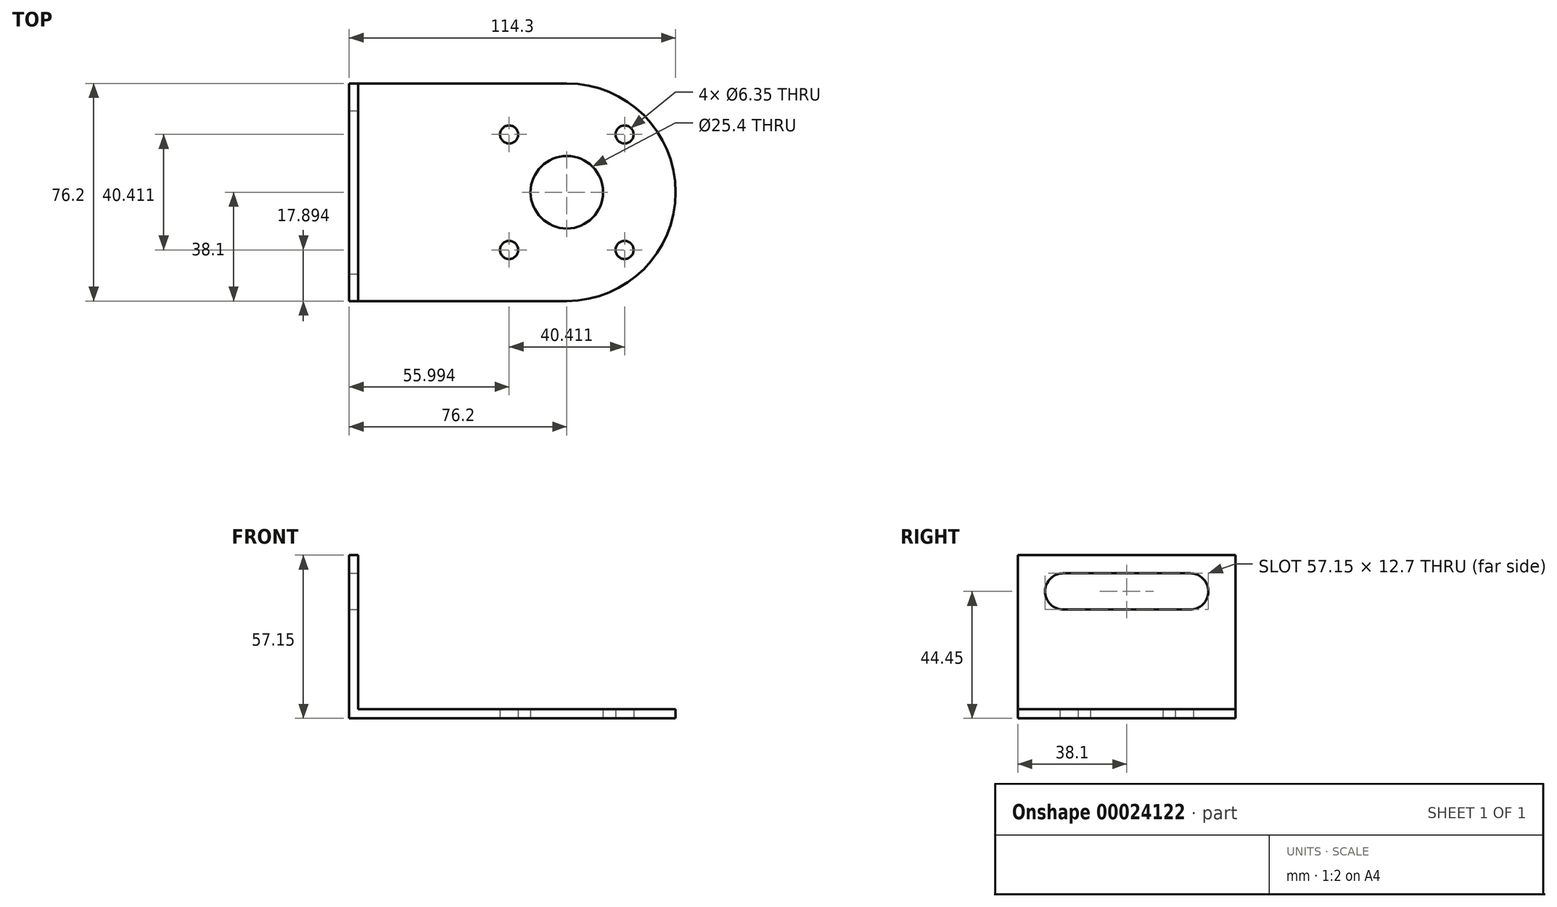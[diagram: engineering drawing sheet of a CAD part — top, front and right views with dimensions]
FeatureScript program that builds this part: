
annotation { "Feature Type Name" : "Feature", "Feature Type Description" : "" }
export const myFeature = defineFeature(function(context is Context, id is Id, definition is map)
    precondition{}
    {
        {
            var Q0;
            Q0=qCreatedBy(makeId("Top.planeOp"),FACE);
            var sketch = newSketch(context, id + "F0", { "sketchPlane" : qUnion([Q0])});
            skLineSegment(sketch, "E0", {"start": v(-76.2, 76.2) * mm, "end": v(-76.2, 0) * mm});
            skLineSegment(sketch, "E1", {"start": v(-76.2, 0) * mm, "end": v(0, 0) * mm});
            skLineSegment(sketch, "E2", {"start": v(0, 0) * mm, "end": v(0, 76.2) * mm, "construction": true});
            skLineSegment(sketch, "E3", {"start": v(0, 76.2) * mm, "end": v(-76.2, 76.2) * mm});
            skArc(sketch, "E4", {"start": v(0, 0) * mm, "mid": v(38.1, 38.1) * mm, "end": v(0, 76.2) * mm});
            skCircle(sketch, "E5", {"center": v(0, 38.1) * mm, "radius": 12.7 * mm});
            skCircle(sketch, "E6", {"center": v(0, 38.1) * mm, "radius": 28.58 * mm, "construction": true});
            skLineSegment(sketch, "E7", {"start": v(0, 38.1) * mm, "end": v(36.04, 74.14) * mm, "construction": true});
            skCircle(sketch, "E8", {"center": v(20.2, 58.3) * mm, "radius": 3.18 * mm});
            skCircle(sketch, "E9.1.0", {"center": v(-20.2, 58.3) * mm, "radius": 3.18 * mm});
            skCircle(sketch, "E9.2.0", {"center": v(-20.2, 17.9) * mm, "radius": 3.18 * mm});
            skCircle(sketch, "E9.3.0", {"center": v(20.2, 17.9) * mm, "radius": 3.18 * mm});
            skSolve(sketch);
        }
        {
            var Q0;
            Q0=makeQuery(id+"F0.imprint","IMPRINT",FACE,{"disambiguationData":[TD([[makeQuery(id+"F0.imprint","IMPRINT",EDGE,{"derivedFrom":sQuery(id+"F0.wireOp",EDGE,"E0")}),1.0]])]});
            extrude(context, id + "F1", {"entities" : qUnion([Q0]), "depth" : 3.17 * mm});
        }
        {
            var Q0;
            Q0=makeQuery(id+"F1.opExtrude","CAP_FACE",FACE,{"disambiguationData":[OSD([sQuery(id+"F0.wireOp",EDGE,"E0"),sQuery(id+"F0.wireOp",EDGE,"E1"),sQuery(id+"F0.wireOp",EDGE,"E3"),sQuery(id+"F0.wireOp",EDGE,"E4"),sQuery(id+"F0.wireOp",EDGE,"E5"),sQuery(id+"F0.wireOp",EDGE,"E8"),sQuery(id+"F0.wireOp",EDGE,"E9.1.0"),sQuery(id+"F0.wireOp",EDGE,"E9.2.0"),sQuery(id+"F0.wireOp",EDGE,"E9.3.0")])],"isStart":false});
            var sketch = newSketch(context, id + "F2", { "sketchPlane" : qUnion([Q0])});
            skLineSegment(sketch, "E10", {"start": v(-73.03, 76.2) * mm, "end": v(-73.03, 0) * mm});
            skSolve(sketch);
        }
        {
            var Q0;
            {var subQ1=sQuery(id+"F2.wireOp",EDGE,"E10");Q0=makeQuery(id+"F2.imprint","IMPRINT",FACE,{"disambiguationData":[TD([[makeQuery(id+"F2.imprint","IMPRINT",EDGE,{"derivedFrom":subQ1}),-1.0]])]});}
            extrude(context, id + "F3", {"entities" : qUnion([Q0]), "operationType" : NewBodyOperationType.ADD, "depth" : 53.97 * mm});
        }
        {
            var Q0;
            Q0=makeQuery(id+"F3.opExtrude","SWEPT_FACE",FACE,{"disambiguationData":[OSD([sQuery(id+"F2.wireOp",EDGE,"E10")])]});
            var sketch = newSketch(context, id + "F4", { "sketchPlane" : qUnion([Q0])});
            skLineSegment(sketch, "E11.rect.bottom", {"start": v(60.33, 38.1) * mm, "end": v(15.88, 38.1) * mm});
            skLineSegment(sketch, "E11.rect.top", {"start": v(60.33, 50.8) * mm, "end": v(15.88, 50.8) * mm});
            skPoint(sketch, "E11.rect.middle", {"position": v(38.1, 44.45) * mm});
            skArc(sketch, "E12", {"start": v(15.88, 50.8) * mm, "mid": v(9.52, 44.45) * mm, "end": v(15.88, 38.1) * mm});
            skArc(sketch, "E13", {"start": v(60.33, 38.1) * mm, "mid": v(66.68, 44.45) * mm, "end": v(60.33, 50.8) * mm});
            skSolve(sketch);
        }
        {
            var Q0;
            Q0=makeQuery(id+"F4.imprint","IMPRINT",FACE,{"disambiguationData":[TD([[makeQuery(id+"F4.imprint","IMPRINT",EDGE,{"derivedFrom":sQuery(id+"F4.wireOp",EDGE,"E11.rect.bottom")}),-1.0]])]});
            extrude(context, id + "F5", {"entities" : qUnion([Q0]), "operationType" : NewBodyOperationType.REMOVE, "oppositeDirection" : true, "depth" : 25.4 * mm});
        }
    });
